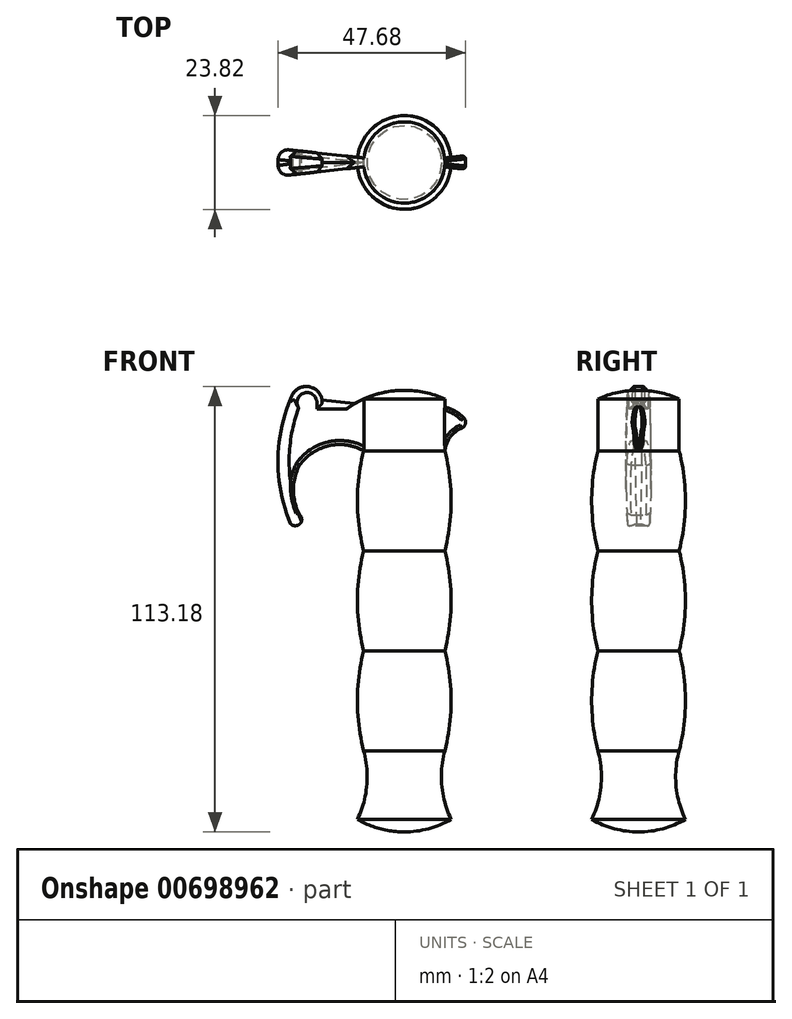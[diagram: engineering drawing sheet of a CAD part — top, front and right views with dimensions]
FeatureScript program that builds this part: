
annotation { "Feature Type Name" : "Feature", "Feature Type Description" : "" }
export const myFeature = defineFeature(function(context is Context, id is Id, definition is map)
    precondition{}
    {
        {
            var Q0;
            Q0=qCreatedBy(makeId("Front.planeOp"),FACE);
            var sketch = newSketch(context, id + "F0", { "sketchPlane" : qUnion([Q0])});
            skArc(sketch, "E0", {"start": v(0, 0) * mm, "mid": v(5.75, -2.37) * mm, "end": v(11.9, -3.17) * mm});
            skArc(sketch, "E1", {"start": v(0, 0) * mm, "mid": v(2.37, 8.59) * mm, "end": v(1.59, 17.46) * mm});
            skArc(sketch, "E2", {"start": v(1.59, 17.46) * mm, "mid": v(6.5, 15.1) * mm, "end": v(11.9, 14.29) * mm});
            skLineSegment(sketch, "E3", {"start": v(11.9, 14.29) * mm, "end": v(11.9, -3.18) * mm});
            skArc(sketch, "E4", {"start": v(1.59, 93.66) * mm, "mid": v(0, 80.96) * mm, "end": v(1.59, 68.26) * mm});
            skArc(sketch, "E5", {"start": v(1.59, 68.26) * mm, "mid": v(0, 55.56) * mm, "end": v(1.59, 42.86) * mm});
            skArc(sketch, "E6", {"start": v(1.59, 42.86) * mm, "mid": v(0, 30.16) * mm, "end": v(1.59, 17.46) * mm});
            skArc(sketch, "E7", {"start": v(11.9, 96.84) * mm, "mid": v(6.5, 96.03) * mm, "end": v(1.59, 93.66) * mm});
            skLineSegment(sketch, "E8", {"start": v(1.59, 93.66) * mm, "end": v(1.59, 106.83) * mm});
            skLineSegment(sketch, "E9", {"start": v(11.9, 106.83) * mm, "end": v(11.9, 14.29) * mm});
            skPoint(sketch, "E10.orphan", {"position": v(22.22, 104.78) * mm});
            skPoint(sketch, "E11.orphan", {"position": v(22.22, 93.66) * mm});
            skLineSegment(sketch, "E12.MirrorCS", {"start": v(22.23, 93.66) * mm, "end": v(22.22, 106.83) * mm});
            skArc(sketch, "E13", {"start": v(28.57, 100.01) * mm, "mid": v(24.28, 97.96) * mm, "end": v(22.22, 93.66) * mm});
            skArc(sketch, "E14", {"start": v(28.57, 100.01) * mm, "mid": v(25.88, 103.03) * mm, "end": v(22.22, 104.78) * mm});
            skPoint(sketch, "E15.MirrorCS.start.orphan", {"position": v(1.59, 93.66) * mm});
            skPoint(sketch, "E16.end.orphan", {"position": v(28.57, 93.66) * mm});
            skLineSegment(sketch, "E17", {"start": v(1.59, 106.83) * mm, "end": v(-9.06, 106.83) * mm});
            skArc(sketch, "E18", {"start": v(-9.06, 106.83) * mm, "mid": v(-13.03, 110) * mm, "end": v(-17, 106.83) * mm});
            skArc(sketch, "E19", {"start": v(-17, 106.83) * mm, "mid": v(-20.17, 90.95) * mm, "end": v(-17, 75.08) * mm});
            skArc(sketch, "E20", {"start": v(-17, 75.08) * mm, "mid": v(-14.75, 75.08) * mm, "end": v(-14.75, 77.32) * mm});
            skArc(sketch, "E21", {"start": v(-14.75, 90.02) * mm, "mid": v(-16.34, 83.67) * mm, "end": v(-14.75, 77.32) * mm});
            skArc(sketch, "E22", {"start": v(1.59, 93.66) * mm, "mid": v(-7.27, 94.94) * mm, "end": v(-14.75, 90.02) * mm});
            skPoint(sketch, "E23.MirrorCS.end.orphan", {"position": v(22.23, 106.83) * mm});
            skPoint(sketch, "E23.MirrorCS.start.orphan", {"position": v(11.9, 109.02) * mm});
            skPoint(sketch, "E24.MirrorCS.start.orphan", {"position": v(11.9, 96.84) * mm});
            skPoint(sketch, "E25.MirrorCS.start.orphan", {"position": v(22.22, 68.26) * mm});
            skPoint(sketch, "E26.MirrorCS.end.orphan", {"position": v(22.23, 17.46) * mm});
            skPoint(sketch, "E26.MirrorCS.start.orphan", {"position": v(22.22, 42.86) * mm});
            skPoint(sketch, "E27.MirrorCS.end.orphan", {"position": v(22.22, 17.46) * mm});
            skPoint(sketch, "E27.MirrorCS.start.orphan", {"position": v(23.81, 0) * mm});
            skPoint(sketch, "E28.MirrorCS.end.orphan", {"position": v(11.9, -3.18) * mm});
            skPoint(sketch, "E29.MirrorCS.end.orphan", {"position": v(11.9, 14.29) * mm});
            skLineSegment(sketch, "E30", {"start": v(1.59, 106.83) * mm, "end": v(11.9, 106.83) * mm});
            skLineSegment(sketch, "E31", {"start": v(11.9, 106.83) * mm, "end": v(11.9, 96.84) * mm});
            skArc(sketch, "E32", {"start": v(22.22, 106.83) * mm, "mid": v(11.9, 109.02) * mm, "end": v(1.59, 106.83) * mm});
            skLineSegment(sketch, "E33", {"start": v(11.9, 109.02) * mm, "end": v(11.9, 106.83) * mm});
            skSolve(sketch);
        }
        {
            var Q0;
            {var subQ0=sQuery(id+"F0.wireOp",EDGE,"E7");Q0=makeQuery(id+"F0.imprint","IMPRINT",FACE,{"disambiguationData":[TD([[makeQuery(id+"F0.imprint","IMPRINT",EDGE,{"derivedFrom":subQ0}),-1.0]])]});}
            var Q1;
            {var subQ0=sQuery(id+"F0.wireOp",EDGE,"E2");Q1=makeQuery(id+"F0.imprint","IMPRINT",FACE,{"disambiguationData":[TD([[makeQuery(id+"F0.imprint","IMPRINT",EDGE,{"derivedFrom":subQ0}),1.0]])]});}
            var Q2;
            Q2=makeQuery(id+"F0.imprint","IMPRINT",FACE,{"disambiguationData":[TD([[makeQuery(id+"F0.imprint","IMPRINT",EDGE,{"derivedFrom":sQuery(id+"F0.wireOp",EDGE,"E0")}),1.0]])]});
            var Q3;
            Q3=sQuery(id+"F0.wireOp",EDGE,"E9");
            revolve(context, id + "F1", {"entities" : qUnion([Q0, Q1, Q2]), "axis" : qUnion([Q3]), "revolveType" : RevolveType.FULL});
        }
        {
            var Q0;
            Q0=makeQuery(id+"F0.imprint","IMPRINT",FACE,{"disambiguationData":[TD([[makeQuery(id+"F0.imprint","IMPRINT",EDGE,{"derivedFrom":sQuery(id+"F0.wireOp",EDGE,"E12.MirrorCS")}),-1.0]])]});
            var Q1;
            Q1=sQuery(id+"F0.wireOp",EDGE,"E9");
            revolve(context, id + "F2", {"operationType" : NewBodyOperationType.ADD, "entities" : qUnion([Q0]), "axis" : qUnion([Q1]), "revolveType" : RevolveType.SYMMETRIC, "angle" : 12.5 * degree, "surfaceOperationType" : NewSurfaceOperationType.NEW});
        }
        {
            var Q0;
            Q0=makeQuery(id+"F0.imprint","IMPRINT",FACE,{"disambiguationData":[TD([[makeQuery(id+"F0.imprint","IMPRINT",EDGE,{"derivedFrom":sQuery(id+"F0.wireOp",EDGE,"E8")}),1.0]])]});
            var Q1;
            Q1=sQuery(id+"F0.wireOp",EDGE,"E31");
            revolve(context, id + "F3", {"operationType" : NewBodyOperationType.ADD, "entities" : qUnion([Q0]), "axis" : qUnion([Q1]), "revolveType" : RevolveType.SYMMETRIC, "oppositeDirection" : true, "angle" : 12.5 * degree, "surfaceOperationType" : NewSurfaceOperationType.NEW});
        }
        {
            var Q0;
            Q0=makeQuery(id+"FlWsBpEJJmEt0rd_1.opFillet","BLEND_EDGE",EDGE,{"blendedFrom":[makeQuery(id+"F2.opRevolve","CAP_EDGE",EDGE,{"disambiguationData":[OSD([sQuery(id+"F0.wireOp",EDGE,"E13")])],"isStart":true}),makeQuery(id+"F2.opRevolve","SWEPT_FACE",FACE,{"disambiguationData":[OSD([sQuery(id+"F0.wireOp",EDGE,"E14")])]})],"blendedInto":[makeQuery(id+"F2.opRevolve","SWEPT_FACE",FACE,{"disambiguationData":[OSD([sQuery(id+"F0.wireOp",EDGE,"E14")])]})]});
            var Q1;
            Q1=makeQuery(id+"F2.opRevolve","SWEPT_EDGE",EDGE,{"disambiguationData":[OSD([sQuery(id+"F0.wireOp",EDGE,"E13"),sQuery(id+"F0.wireOp",EDGE,"E14")])]});
            var Q2;
            Q2=makeQuery(id+"FlWsBpEJJmEt0rd_1.opFillet","BLEND_EDGE",EDGE,{"blendedFrom":[makeQuery(id+"F2.opRevolve","CAP_EDGE",EDGE,{"disambiguationData":[OSD([sQuery(id+"F0.wireOp",EDGE,"E13")])],"isStart":false}),makeQuery(id+"F2.opRevolve","SWEPT_FACE",FACE,{"disambiguationData":[OSD([sQuery(id+"F0.wireOp",EDGE,"E14")])]})],"blendedInto":[makeQuery(id+"F2.opRevolve","SWEPT_FACE",FACE,{"disambiguationData":[OSD([sQuery(id+"F0.wireOp",EDGE,"E14")])]})]});
            fillet(context, id + "F4", {"entities" : qUnion([Q0, Q1, Q2]), "radius" : 1.52 * mm, "tangentPropagation" : true, "allowEdgeOverflow" : false});
        }
        {
            var Q0;
            {var subQ0=sQuery(id+"F0.wireOp",EDGE,"E30");Q0=makeQuery(id+"F0.imprint","IMPRINT",FACE,{"disambiguationData":[TD([[makeQuery(id+"F0.imprint","IMPRINT",EDGE,{"derivedFrom":subQ0}),1.0]])]});}
            var Q1;
            Q1=sQuery(id+"F0.wireOp",EDGE,"E9");
            revolve(context, id + "F5", {"operationType" : NewBodyOperationType.ADD, "surfaceOperationType" : NewSurfaceOperationType.NEW, "entities" : qUnion([Q0]), "axis" : qUnion([Q1]), "revolveType" : RevolveType.FULL});
        }
        {
            var Q0;
            Q0=makeQuery(id+"F3.opRevolve","CAP_EDGE",EDGE,{"disambiguationData":[OSD([sQuery(id+"F0.wireOp",EDGE,"E19")])],"isStart":false});
            var Q1;
            Q1=makeQuery(id+"F3.opRevolve","CAP_EDGE",EDGE,{"disambiguationData":[OSD([sQuery(id+"F0.wireOp",EDGE,"E19")])],"isStart":true});
            fillet(context, id + "F6", {"entities" : qUnion([Q0, Q1]), "radius" : 2.54 * mm, "tangentPropagation" : true, "allowEdgeOverflow" : false});
        }
        {
            var Q0;
            Q0=makeQuery(id+"F3.opRevolve","CAP_EDGE",EDGE,{"disambiguationData":[OSD([sQuery(id+"F0.wireOp",EDGE,"E18")])],"isStart":false});
            var Q1;
            Q1=makeQuery(id+"F3.opRevolve","CAP_EDGE",EDGE,{"disambiguationData":[OSD([sQuery(id+"F0.wireOp",EDGE,"E18")])],"isStart":true});
            chamfer(context, id + "F7", {"entities" : qUnion([Q0, Q1]), "width" : 1.52 * mm, "tangentPropagation" : true});
        }
        {
            var Q0;
            Q0=makeQuery(id+"F3.opRevolve","CAP_EDGE",EDGE,{"disambiguationData":[OSD([sQuery(id+"F0.wireOp",EDGE,"E22")])],"isStart":false});
            var Q1;
            Q1=makeQuery(id+"F3.opRevolve","CAP_EDGE",EDGE,{"disambiguationData":[OSD([sQuery(id+"F0.wireOp",EDGE,"E22")])],"isStart":true});
            var Q2;
            Q2=makeQuery(id+"F3.opRevolve","CAP_EDGE",EDGE,{"disambiguationData":[OSD([sQuery(id+"F0.wireOp",EDGE,"E21")])],"isStart":false});
            var Q3;
            Q3=makeQuery(id+"F3.opRevolve","CAP_EDGE",EDGE,{"disambiguationData":[OSD([sQuery(id+"F0.wireOp",EDGE,"E21")])],"isStart":true});
            fillet(context, id + "F8", {"entities" : qUnion([Q0, Q1, Q2, Q3]), "radius" : 1.02 * mm, "tangentPropagation" : true, "allowEdgeOverflow" : false});
        }
        {
            var Q0;
            {var subQ0=sQuery(id+"F0.wireOp",EDGE,"E14");var subQ1=sQuery(id+"F0.wireOp",EDGE,"E13");Q0=makeQuery(id+"F4.opFillet","BLEND_EDGE",EDGE,{"blendedFrom":[makeQuery(id+"F2.opRevolve","SWEPT_EDGE",EDGE,{"disambiguationData":[OSD([subQ1,subQ0])]}),makeQuery(id+"F2.opRevolve","CAP_FACE",FACE,{"disambiguationData":[OSD([sQuery(id+"F0.wireOp",EDGE,"E12.MirrorCS"),subQ1,subQ0])],"isStart":false})],"blendedInto":[makeQuery(id+"F2.opRevolve","CAP_FACE",FACE,{"disambiguationData":[OSD([sQuery(id+"F0.wireOp",EDGE,"E12.MirrorCS"),subQ1,subQ0])],"isStart":false})]});}
            var Q1;
            {var subQ0=sQuery(id+"F0.wireOp",EDGE,"E14");var subQ1=sQuery(id+"F0.wireOp",EDGE,"E13");Q1=makeQuery(id+"F4.opFillet","BLEND_EDGE",EDGE,{"blendedFrom":[makeQuery(id+"F2.opRevolve","SWEPT_EDGE",EDGE,{"disambiguationData":[OSD([subQ1,subQ0])]}),makeQuery(id+"F2.opRevolve","CAP_FACE",FACE,{"disambiguationData":[OSD([sQuery(id+"F0.wireOp",EDGE,"E12.MirrorCS"),subQ1,subQ0])],"isStart":true})],"blendedInto":[makeQuery(id+"F2.opRevolve","CAP_FACE",FACE,{"disambiguationData":[OSD([sQuery(id+"F0.wireOp",EDGE,"E12.MirrorCS"),subQ1,subQ0])],"isStart":true})]});}
            fillet(context, id + "F9", {"entities" : qUnion([Q0, Q1]), "radius" : 0.76 * mm, "tangentPropagation" : true, "allowEdgeOverflow" : false});
        }
        {
            var Q0;
            Q0=makeQuery(id+"F3.opRevolve","CAP_EDGE",EDGE,{"disambiguationData":[OSD([sQuery(id+"F0.wireOp",EDGE,"E17")])],"isStart":false});
            var Q1;
            Q1=makeQuery(id+"F3.opRevolve","CAP_EDGE",EDGE,{"disambiguationData":[OSD([sQuery(id+"F0.wireOp",EDGE,"E17")])],"isStart":true});
            chamfer(context, id + "F10", {"entities" : qUnion([Q0, Q1]), "width" : 2.54 * mm, "tangentPropagation" : true});
        }
    });
